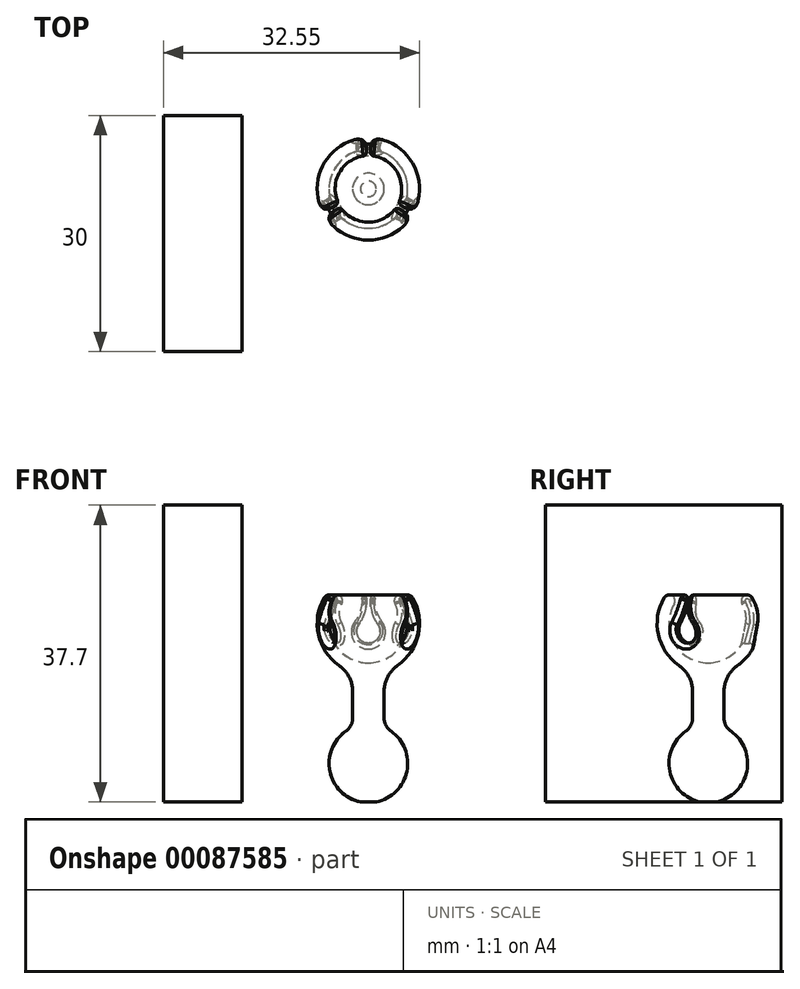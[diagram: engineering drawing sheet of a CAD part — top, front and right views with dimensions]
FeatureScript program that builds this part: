
annotation { "Feature Type Name" : "Feature", "Feature Type Description" : "" }
export const myFeature = defineFeature(function(context is Context, id is Id, definition is map)
    precondition{}
    {
        {
            var Q0;
            Q0=qCreatedBy(makeId("Front.planeOp"),FACE);
            var sketch = newSketch(context, id + "F0", { "sketchPlane" : qUnion([Q0])});
            skArc(sketch, "E0", {"start": v(-4.33, 2.5) * mm, "mid": v(-4.33, -2.5) * mm, "end": v(0, -5) * mm});
            skArc(sketch, "E1", {"start": v(-5.63, 3.25) * mm, "mid": v(-6.07, -2.33) * mm, "end": v(-2, -6.18) * mm});
            skLineSegment(sketch, "E2", {"start": v(-4.33, 2.5) * mm, "end": v(-5.63, 3.25) * mm, "construction": true});
            skLineSegment(sketch, "E3", {"start": v(0, -5) * mm, "end": v(0, -13.57) * mm, "construction": true});
            skArc(sketch, "E4", {"start": v(-4.33, 2.5) * mm, "mid": v(-4.6, 3.52) * mm, "end": v(-5.63, 3.25) * mm});
            skPoint(sketch, "E5.endSnap0", {"position": v(0, -6.78) * mm});
            skLineSegment(sketch, "E6.trimOffspring", {"start": v(0, -5) * mm, "end": v(0, -6.5) * mm});
            skLineSegment(sketch, "E7", {"start": v(-2, -6.18) * mm, "end": v(-2, -13.18) * mm});
            skLineSegment(sketch, "E8", {"start": v(0, -15) * mm, "end": v(0, -6.5) * mm});
            skArc(sketch, "E9", {"start": v(-2, -13.18) * mm, "mid": v(-4.97, -18.3) * mm, "end": v(-1, -22.67) * mm});
            skLineSegment(sketch, "E10", {"start": v(0, -15) * mm, "end": v(0, -22.77) * mm});
            skLineSegment(sketch, "E11", {"start": v(-1, -22.67) * mm, "end": v(0, -22.67) * mm});
            skCircle(sketch, "E12", {"center": v(0, 5.75) * mm, "radius": 5 * mm, "construction": true});
            skLineSegment(sketch, "E13", {"start": v(-5, 15.12) * mm, "end": v(-5, -21.33) * mm, "construction": true});
            skCircle(sketch, "E14", {"center": v(0, 0) * mm, "radius": 5 * mm, "construction": true});
            skLineSegment(sketch, "E15", {"start": v(-4.33, 2.5) * mm, "end": v(-4.33, -8.35) * mm, "construction": true});
            skSolve(sketch);
        }
        {
            var Q0;
            Q0=makeQuery(id+"F0.imprint","IMPRINT",FACE,{"disambiguationData":[TD([[makeQuery(id+"F0.imprint","IMPRINT",EDGE,{"derivedFrom":sQuery(id+"F0.wireOp",EDGE,"E0")}),-1.0]])]});
            var Q1;
            Q1=sQuery(id+"F0.wireOp",EDGE,"E8");
            revolve(context, id + "F1", {"entities" : qUnion([Q0]), "axis" : qUnion([Q1]), "revolveType" : RevolveType.FULL});
        }
        {
            var Q0;
            Q0=qCreatedBy(makeId("Top.planeOp"),FACE);
            cPlane(context, id + "F2", {"entities" : qUnion([Q0]), "cplaneType" : CPlaneType.OFFSET, "offset" : 1 * mm, "oppositeDirection" : true, "width" : 150 * mm, "height" : 150 * mm});
        }
        {
            var Q0;
            Q0=qCreatedBy(id+"F2.planeOp",FACE);
            var sketch = newSketch(context, id + "F3", { "sketchPlane" : qUnion([Q0])});
            skLineSegment(sketch, "E16", {"start": v(0, 0) * mm, "end": v(0, 14.2) * mm, "construction": true});
            skLineSegment(sketch, "E17.bottom", {"start": v(1.5, 14.2) * mm, "end": v(-1.5, 14.2) * mm});
            skLineSegment(sketch, "E17.top", {"start": v(1.5, 0) * mm, "end": v(-1.5, 0) * mm});
            skLineSegment(sketch, "E17.left", {"start": v(1.5, 14.2) * mm, "end": v(1.5, 0) * mm});
            skLineSegment(sketch, "E17.right", {"start": v(-1.5, 14.2) * mm, "end": v(-1.5, 0) * mm});
            skPoint(sketch, "E17.middle", {"position": v(0, 7.1) * mm});
            skPoint(sketch, "E18.1.0", {"position": v(-6.15, -3.55) * mm});
            skLineSegment(sketch, "E18.1.1", {"start": v(-11.55, -8.4) * mm, "end": v(0.75, -1.3) * mm});
            skLineSegment(sketch, "E18.1.2", {"start": v(-13.05, -5.8) * mm, "end": v(-0.75, 1.3) * mm});
            skLineSegment(sketch, "E18.1.3", {"start": v(-0.75, 1.3) * mm, "end": v(0.75, -1.3) * mm});
            skLineSegment(sketch, "E18.1.4", {"start": v(0, 0) * mm, "end": v(-12.3, -7.1) * mm, "construction": true});
            skLineSegment(sketch, "E18.1.5", {"start": v(-13.05, -5.8) * mm, "end": v(-11.55, -8.4) * mm});
            skPoint(sketch, "E18.2.0", {"position": v(6.15, -3.55) * mm});
            skLineSegment(sketch, "E18.2.1", {"start": v(13.05, -5.8) * mm, "end": v(0.75, 1.3) * mm});
            skLineSegment(sketch, "E18.2.2", {"start": v(11.55, -8.4) * mm, "end": v(-0.75, -1.3) * mm});
            skLineSegment(sketch, "E18.2.3", {"start": v(-0.75, -1.3) * mm, "end": v(0.75, 1.3) * mm});
            skLineSegment(sketch, "E18.2.4", {"start": v(0, 0) * mm, "end": v(12.3, -7.1) * mm, "construction": true});
            skLineSegment(sketch, "E18.2.5", {"start": v(11.55, -8.4) * mm, "end": v(13.05, -5.8) * mm});
            skPoint(sketch, "E18.center", {"position": v(0, 0) * mm});
            skSolve(sketch);
        }
        {
            var Q0;
            Q0=qSketchRegion(id+"F3",true);
            extrude(context, id + "F4", {"entities" : qUnion([Q0]), "operationType" : NewBodyOperationType.REMOVE, "endBound" : BoundingType.SYMMETRIC, "oppositeDirection" : true, "depth" : 3 * mm});
        }
        {
            var Q0;
            Q0=makeQuery(id+"F4.boolean.opBoolean","COPY",EDGE,{"derivedFrom":makeQuery(id+"F4.opExtrude","CAP_EDGE",EDGE,{"disambiguationData":[OSD([sQuery(id+"F3.wireOp",EDGE,"E18.1.2")])],"isStart":false})});
            var Q1;
            Q1=makeQuery(id+"F4.boolean.opBoolean","COPY",EDGE,{"derivedFrom":makeQuery(id+"F4.opExtrude","CAP_EDGE",EDGE,{"disambiguationData":[OSD([sQuery(id+"F3.wireOp",EDGE,"E18.1.1")])],"isStart":false})});
            var Q2;
            Q2=makeQuery(id+"F4.boolean.opBoolean","COPY",EDGE,{"derivedFrom":makeQuery(id+"F4.opExtrude","CAP_EDGE",EDGE,{"disambiguationData":[OSD([sQuery(id+"F3.wireOp",EDGE,"E18.2.1")])],"isStart":false})});
            var Q3;
            Q3=makeQuery(id+"F4.boolean.opBoolean","COPY",EDGE,{"derivedFrom":makeQuery(id+"F4.opExtrude","CAP_EDGE",EDGE,{"disambiguationData":[OSD([sQuery(id+"F3.wireOp",EDGE,"E18.2.2")])],"isStart":false})});
            var Q4;
            Q4=makeQuery(id+"F4.boolean.opBoolean","COPY",EDGE,{"derivedFrom":makeQuery(id+"F4.opExtrude","CAP_EDGE",EDGE,{"disambiguationData":[OSD([sQuery(id+"F3.wireOp",EDGE,"E17.right")])],"isStart":false})});
            var Q5;
            Q5=makeQuery(id+"F4.boolean.opBoolean","COPY",EDGE,{"derivedFrom":makeQuery(id+"F4.opExtrude","CAP_EDGE",EDGE,{"disambiguationData":[OSD([sQuery(id+"F3.wireOp",EDGE,"E17.left")])],"isStart":false})});
            var Q6;
            Q6=makeQuery(id+"F4.boolean.opBoolean","COPY",EDGE,{"derivedFrom":makeQuery(id+"F4.opExtrude","CAP_EDGE",EDGE,{"disambiguationData":[OSD([sQuery(id+"F3.wireOp",EDGE,"E18.2.1")])],"isStart":true})});
            var Q7;
            Q7=makeQuery(id+"F4.boolean.opBoolean","COPY",EDGE,{"derivedFrom":makeQuery(id+"F4.opExtrude","CAP_EDGE",EDGE,{"disambiguationData":[OSD([sQuery(id+"F3.wireOp",EDGE,"E18.2.2")])],"isStart":true})});
            var Q8;
            Q8=makeQuery(id+"F4.boolean.opBoolean","COPY",EDGE,{"derivedFrom":makeQuery(id+"F4.opExtrude","CAP_EDGE",EDGE,{"disambiguationData":[OSD([sQuery(id+"F3.wireOp",EDGE,"E17.left")])],"isStart":true})});
            var Q9;
            Q9=makeQuery(id+"F4.boolean.opBoolean","COPY",EDGE,{"derivedFrom":makeQuery(id+"F4.opExtrude","CAP_EDGE",EDGE,{"disambiguationData":[OSD([sQuery(id+"F3.wireOp",EDGE,"E17.right")])],"isStart":true})});
            var Q10;
            Q10=makeQuery(id+"F4.boolean.opBoolean","COPY",EDGE,{"derivedFrom":makeQuery(id+"F4.opExtrude","CAP_EDGE",EDGE,{"disambiguationData":[OSD([sQuery(id+"F3.wireOp",EDGE,"E18.1.1")])],"isStart":true})});
            var Q11;
            Q11=makeQuery(id+"F4.boolean.opBoolean","COPY",EDGE,{"derivedFrom":makeQuery(id+"F4.opExtrude","CAP_EDGE",EDGE,{"disambiguationData":[OSD([sQuery(id+"F3.wireOp",EDGE,"E18.1.2")])],"isStart":true})});
            fillet(context, id + "F5", {"entities" : qUnion([Q0, Q1, Q2, Q3, Q4, Q5, Q6, Q7, Q8, Q9, Q10, Q11]), "radius" : 1.5 * mm, "tangentPropagation" : true, "allowEdgeOverflow" : false});
        }
        {
            var Q0;
            Q0=makeQuery(id+"F1.opRevolve","SWEPT_EDGE",EDGE,{"disambiguationData":[OSD([sQuery(id+"F0.wireOp",EDGE,"E1"),sQuery(id+"F0.wireOp",EDGE,"E7")])]});
            fillet(context, id + "F6", {"entities" : qUnion([Q0]), "radius" : 4 * mm, "tangentPropagation" : true, "allowEdgeOverflow" : false});
        }
        {
            var Q0;
            Q0=makeQuery(id+"F1.opRevolve","SWEPT_EDGE",EDGE,{"disambiguationData":[OSD([sQuery(id+"F0.wireOp",EDGE,"E7"),sQuery(id+"F0.wireOp",EDGE,"ywg5SL3T-TYOw-sGt6-3Rzi-PARAZnVLxAsf")])]});
            fillet(context, id + "F7", {"entities" : qUnion([Q0]), "radius" : 2 * mm, "tangentPropagation" : true, "allowEdgeOverflow" : false});
        }
        {
            var Q0;
            Q0=makeQuery(id+"F1.opRevolve","SWEPT_FACE",FACE,{"disambiguationData":[OSD([sQuery(id+"F0.wireOp",EDGE,"E11")])]});
            var sketch = newSketch(context, id + "F8", { "sketchPlane" : qUnion([Q0])});
            skLineSegment(sketch, "E19.bottom", {"start": v(-26.05, -9.32) * mm, "end": v(-16.05, -9.32) * mm});
            skLineSegment(sketch, "E19.top", {"start": v(-26.05, 20.68) * mm, "end": v(-16.05, 20.68) * mm});
            skLineSegment(sketch, "E19.left", {"start": v(-26.05, -9.32) * mm, "end": v(-26.05, 20.68) * mm});
            skLineSegment(sketch, "E19.right", {"start": v(-16.05, -9.32) * mm, "end": v(-16.05, 20.68) * mm});
            skSolve(sketch);
        }
        {
            var Q0;
            Q0=makeQuery(id+"F8.imprint","IMPRINT",FACE,{"disambiguationData":[TD([[makeQuery(id+"F8.imprint","IMPRINT",EDGE,{"derivedFrom":sQuery(id+"F8.wireOp",EDGE,"E19.bottom")}),1.0]])]});
            extrude(context, id + "F9", {"entities" : qUnion([Q0]), "oppositeDirection" : true, "depth" : 37.7 * mm});
        }
        {
            var Q0;
            Q0=qCreatedBy(id+"F2.planeOp",FACE);
            var sketch = newSketch(context, id + "F10", { "sketchPlane" : qUnion([Q0])});
            skLineSegment(sketch, "E20.0", {"start": v(0, 0) * mm, "end": v(0, 14.2) * mm, "construction": true});
            skLineSegment(sketch, "E21.bottom", {"start": v(0.25, 3.44) * mm, "end": v(-0.25, 3.44) * mm});
            skLineSegment(sketch, "E21.top", {"start": v(0.25, 10.76) * mm, "end": v(-0.25, 10.76) * mm});
            skLineSegment(sketch, "E21.left", {"start": v(0.25, 3.44) * mm, "end": v(0.25, 10.76) * mm});
            skLineSegment(sketch, "E21.right", {"start": v(-0.25, 3.44) * mm, "end": v(-0.25, 10.76) * mm});
            skPoint(sketch, "E21.middle", {"position": v(0, 7.1) * mm});
            skLineSegment(sketch, "E22.1.0", {"start": v(-2.86, -1.94) * mm, "end": v(-9.2, -5.6) * mm});
            skLineSegment(sketch, "E22.1.1", {"start": v(-3.1, -1.5) * mm, "end": v(-9.44, -5.16) * mm});
            skPoint(sketch, "E22.1.2", {"position": v(-6.15, -3.55) * mm});
            skLineSegment(sketch, "E22.1.3", {"start": v(0, 0) * mm, "end": v(-12.3, -7.1) * mm, "construction": true});
            skLineSegment(sketch, "E22.1.4", {"start": v(-9.44, -5.16) * mm, "end": v(-9.2, -5.6) * mm});
            skLineSegment(sketch, "E22.1.5", {"start": v(-3.1, -1.5) * mm, "end": v(-2.86, -1.94) * mm});
            skLineSegment(sketch, "E22.2.0", {"start": v(3.1, -1.5) * mm, "end": v(9.44, -5.16) * mm});
            skLineSegment(sketch, "E22.2.1", {"start": v(2.86, -1.94) * mm, "end": v(9.2, -5.6) * mm});
            skPoint(sketch, "E22.2.2", {"position": v(6.15, -3.55) * mm});
            skLineSegment(sketch, "E22.2.3", {"start": v(0, 0) * mm, "end": v(12.3, -7.1) * mm, "construction": true});
            skLineSegment(sketch, "E22.2.4", {"start": v(9.2, -5.6) * mm, "end": v(9.44, -5.16) * mm});
            skLineSegment(sketch, "E22.2.5", {"start": v(2.86, -1.94) * mm, "end": v(3.1, -1.5) * mm});
            skPoint(sketch, "E22.center", {"position": v(0, 0) * mm});
            skSolve(sketch);
        }
        {
            var Q0;
            Q0 = qSketchRegion(id + "F10", true);
            extrude(context, id + "F11", {"entities" : qUnion([Q0]), "operationType" : NewBodyOperationType.REMOVE, "depth" : 25 * mm});
        }
        {
            var Q0;
            Q0=makeQuery(id+"F11.boolean.opBoolean","INTERSECT",EDGE,{"derivedFrom":[makeQuery(id+"F5.opFillet","BLEND_FACE",FACE,{"disambiguationData":[OSD([sQuery(id+"F3.wireOp",EDGE,"E18.1.1")])]}),makeQuery(id+"F11.opExtrude","SWEPT_FACE",FACE,{"disambiguationData":[OSD([sQuery(id+"F10.wireOp",EDGE,"E22.1.1")])]})]});
            var Q1;
            Q1=makeQuery(id+"F11.boolean.opBoolean","INTERSECT",EDGE,{"derivedFrom":[makeQuery(id+"F5.opFillet","BLEND_FACE",FACE,{"disambiguationData":[OSD([sQuery(id+"F3.wireOp",EDGE,"E18.1.1")])]}),makeQuery(id+"F11.opExtrude","SWEPT_FACE",FACE,{"disambiguationData":[OSD([sQuery(id+"F10.wireOp",EDGE,"E22.1.0")])]})]});
            var Q2;
            Q2=makeQuery(id+"F11.boolean.opBoolean","INTERSECT",EDGE,{"derivedFrom":[makeQuery(id+"F5.opFillet","BLEND_FACE",FACE,{"disambiguationData":[OSD([sQuery(id+"F3.wireOp",EDGE,"E18.2.1")])]}),makeQuery(id+"F11.opExtrude","SWEPT_FACE",FACE,{"disambiguationData":[OSD([sQuery(id+"F10.wireOp",EDGE,"E22.2.0")])]})]});
            var Q3;
            Q3=makeQuery(id+"F11.boolean.opBoolean","INTERSECT",EDGE,{"derivedFrom":[makeQuery(id+"F5.opFillet","BLEND_FACE",FACE,{"disambiguationData":[OSD([sQuery(id+"F3.wireOp",EDGE,"E18.2.1")])]}),makeQuery(id+"F11.opExtrude","SWEPT_FACE",FACE,{"disambiguationData":[OSD([sQuery(id+"F10.wireOp",EDGE,"E22.2.1")])]})]});
            var Q4;
            Q4=makeQuery(id+"F11.boolean.opBoolean","INTERSECT",EDGE,{"derivedFrom":[makeQuery(id+"F5.opFillet","BLEND_FACE",FACE,{"disambiguationData":[OSD([sQuery(id+"F3.wireOp",EDGE,"E17.left")])]}),makeQuery(id+"F11.opExtrude","SWEPT_FACE",FACE,{"disambiguationData":[OSD([sQuery(id+"F10.wireOp",EDGE,"E21.left")])]})]});
            var Q5;
            Q5=makeQuery(id+"F11.boolean.opBoolean","INTERSECT",EDGE,{"derivedFrom":[makeQuery(id+"F5.opFillet","BLEND_FACE",FACE,{"disambiguationData":[OSD([sQuery(id+"F3.wireOp",EDGE,"E17.left")])]}),makeQuery(id+"F11.opExtrude","SWEPT_FACE",FACE,{"disambiguationData":[OSD([sQuery(id+"F10.wireOp",EDGE,"E21.right")])]})]});
            fillet(context, id + "F12", {"entities" : qUnion([Q0, Q1, Q2, Q3, Q4, Q5]), "radius" : 5 * mm, "tangentPropagation" : true, "allowEdgeOverflow" : false});
        }
        {
            var Q0;
            Q0=makeQuery(id+"F12.opFillet","BLEND_EDGE",EDGE,{"blendedFrom":[makeQuery(id+"F11.boolean.opBoolean","INTERSECT",EDGE,{"derivedFrom":[makeQuery(id+"F5.opFillet","BLEND_FACE",FACE,{"disambiguationData":[OSD([sQuery(id+"F3.wireOp",EDGE,"E18.1.1")])]}),makeQuery(id+"F11.opExtrude","SWEPT_FACE",FACE,{"disambiguationData":[OSD([sQuery(id+"F10.wireOp",EDGE,"E22.1.1")])]})]}),makeQuery(id+"F1.opRevolve","SWEPT_FACE",FACE,{"disambiguationData":[OSD([sQuery(id+"F0.wireOp",EDGE,"E1")])]})],"blendedInto":[makeQuery(id+"F1.opRevolve","SWEPT_FACE",FACE,{"disambiguationData":[OSD([sQuery(id+"F0.wireOp",EDGE,"E1")])]})]});
            var Q1;
            Q1=makeQuery(id+"F11.boolean.opBoolean","INTERSECT",EDGE,{"derivedFrom":[makeQuery(id+"F1.opRevolve","SWEPT_FACE",FACE,{"disambiguationData":[OSD([sQuery(id+"F0.wireOp",EDGE,"E1")])]}),makeQuery(id+"F11.opExtrude","SWEPT_FACE",FACE,{"disambiguationData":[OSD([sQuery(id+"F10.wireOp",EDGE,"E21.right")])]})]});
            var Q2;
            Q2=makeQuery(id+"F11.boolean.opBoolean","INTERSECT",EDGE,{"derivedFrom":[makeQuery(id+"F1.opRevolve","SWEPT_FACE",FACE,{"disambiguationData":[OSD([sQuery(id+"F0.wireOp",EDGE,"E1")])]}),makeQuery(id+"F11.opExtrude","SWEPT_FACE",FACE,{"disambiguationData":[OSD([sQuery(id+"F10.wireOp",EDGE,"E22.2.0")])]})]});
            fillet(context, id + "F13", {"entities" : qUnion([Q0, Q1, Q2]), "radius" : .5 * mm, "tangentPropagation" : true, "allowEdgeOverflow" : false});
        }
    });
